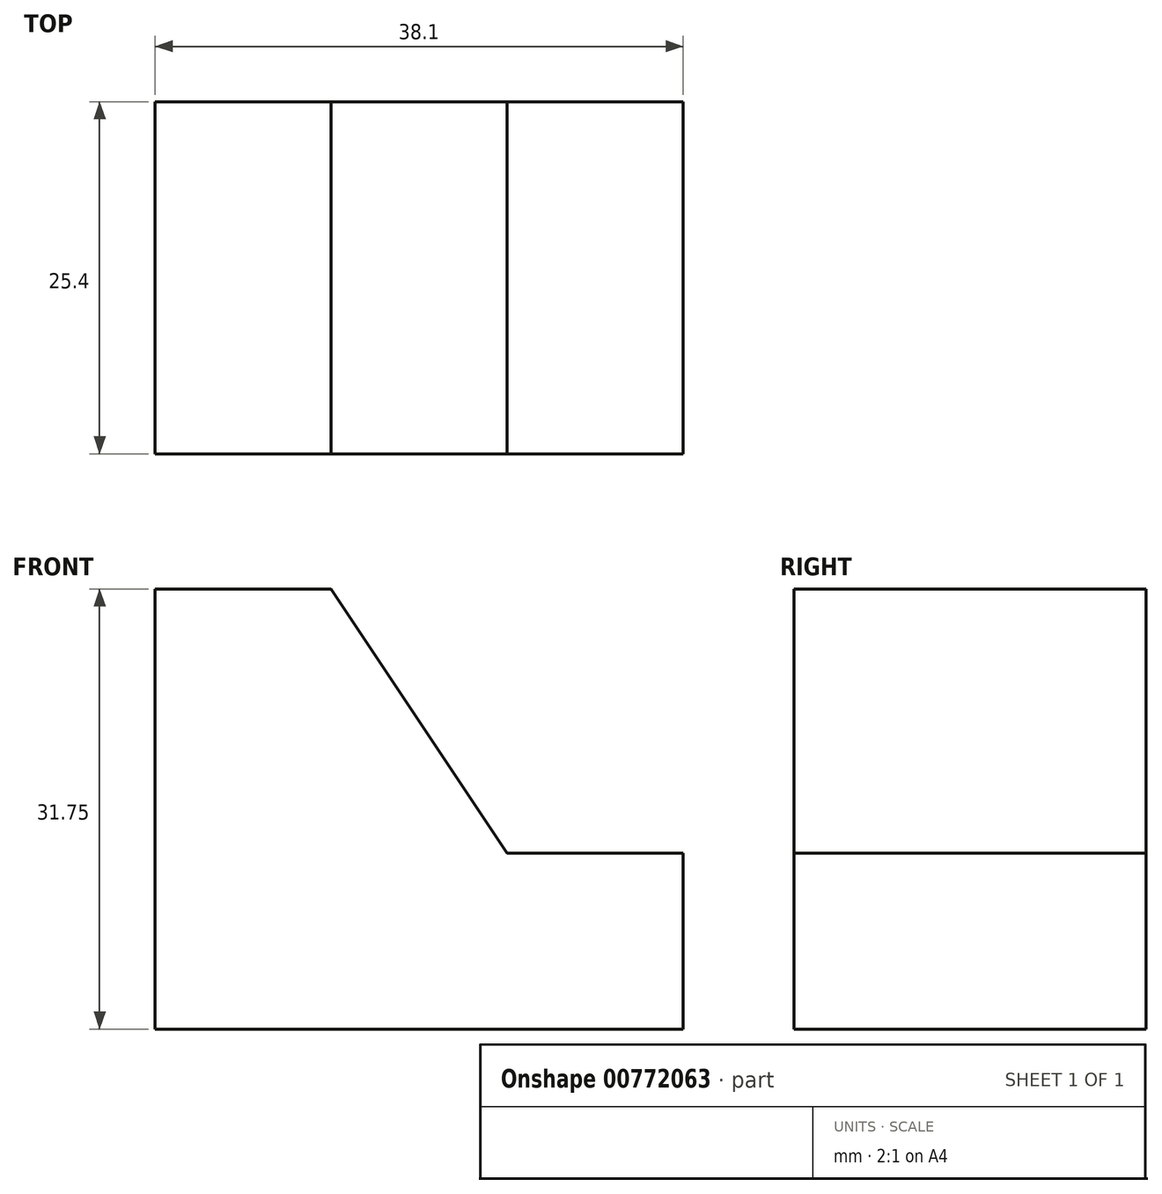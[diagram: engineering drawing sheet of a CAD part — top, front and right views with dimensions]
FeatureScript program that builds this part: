
annotation { "Feature Type Name" : "Feature", "Feature Type Description" : "" }
export const myFeature = defineFeature(function(context is Context, id is Id, definition is map)
    precondition{}
    {
        {
            var Q0;
            Q0=qCreatedBy(makeId("Front.planeOp"),FACE);
            var sketch = newSketch(context, id + "F0", { "sketchPlane" : qUnion([Q0])});
            skLineSegment(sketch, "E0", {"start": v(0, 0) * mm, "end": v(0, 12.7) * mm});
            skLineSegment(sketch, "E1", {"start": v(0, 12.7) * mm, "end": v(-12.7, 12.7) * mm});
            skLineSegment(sketch, "E2", {"start": v(0, 0) * mm, "end": v(-38.1, 0) * mm});
            skLineSegment(sketch, "E3", {"start": v(-38.1, 0) * mm, "end": v(-38.1, 31.75) * mm});
            skLineSegment(sketch, "E4", {"start": v(-38.1, 31.75) * mm, "end": v(-25.4, 31.75) * mm});
            skLineSegment(sketch, "E5", {"start": v(-25.4, 31.75) * mm, "end": v(-12.7, 12.7) * mm});
            skSolve(sketch);
        }
        {
            var Q0;
            Q0=makeQuery(id+"F0.imprint","IMPRINT",FACE,{"disambiguationData":[TD([[makeQuery(id+"F0.imprint","IMPRINT",EDGE,{"derivedFrom":sQuery(id+"F0.wireOp",EDGE,"E0")}),1.0]])]});
            extrude(context, id + "F1", {"entities" : qUnion([Q0]), "depth" : 25.4 * mm, "offsetDistance" : 25.4 * mm});
        }
    });
